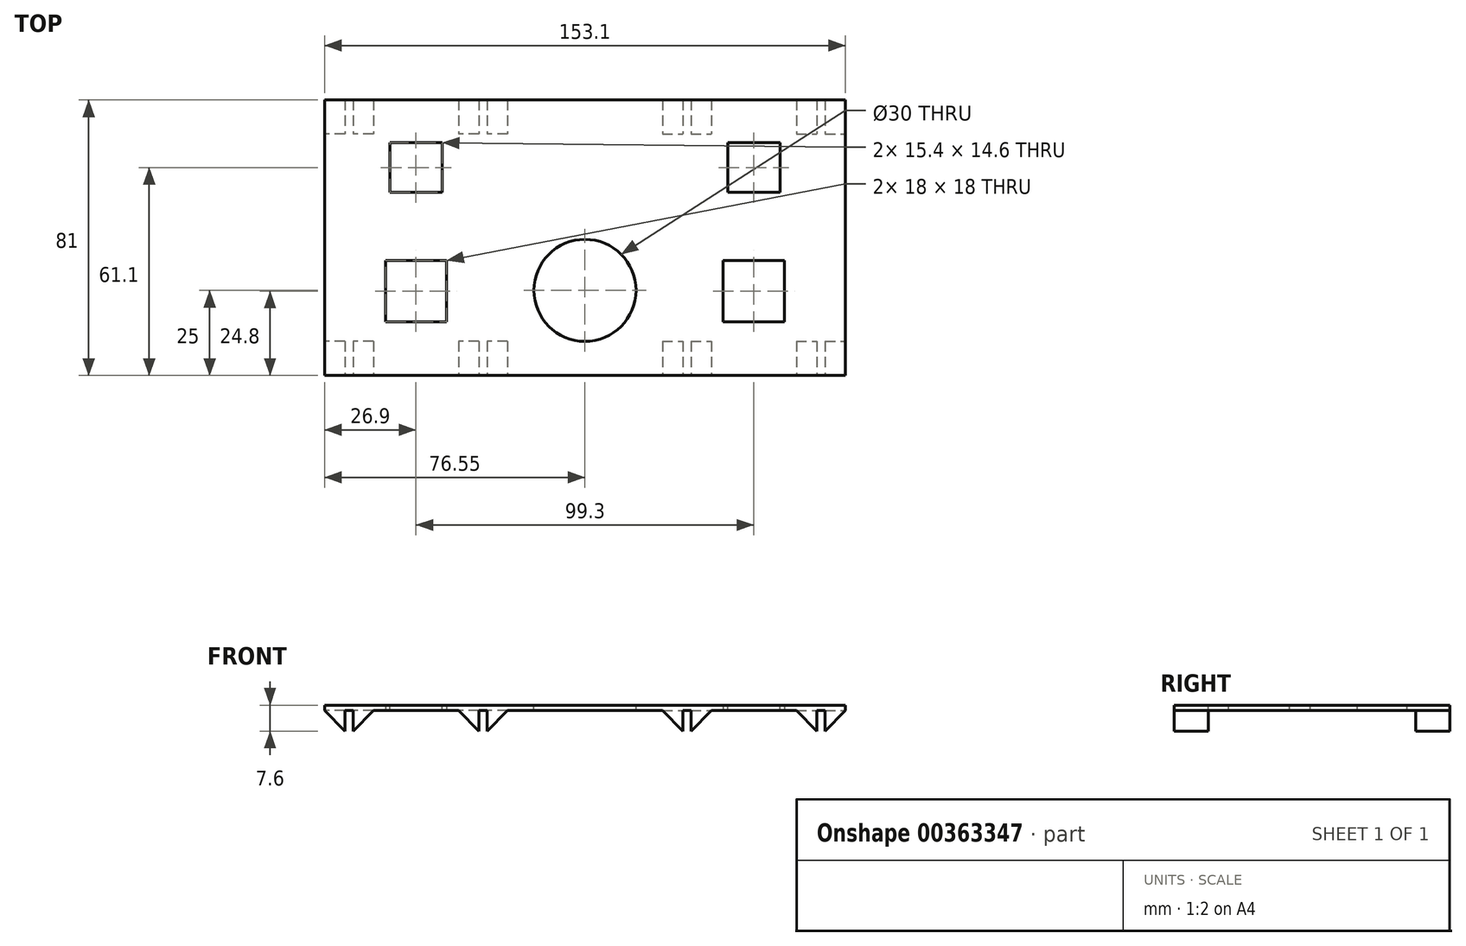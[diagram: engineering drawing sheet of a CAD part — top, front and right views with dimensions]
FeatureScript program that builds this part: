
annotation { "Feature Type Name" : "Feature", "Feature Type Description" : "" }
export const myFeature = defineFeature(function(context is Context, id is Id, definition is map)
    precondition{}
    {
        {
            var Q0;
            Q0=qCreatedBy(makeId("Front.planeOp"),FACE);
            cPlane(context, id + "F0", {"entities" : qUnion([Q0]), "cplaneType" : CPlaneType.OFFSET, "offset" : 40.5 * mm, "width" : 150 * mm, "height" : 150 * mm});
        }
        {
            var Q0;
            Q0=qCreatedBy(id+"F0.planeOp",FACE);
            var sketch = newSketch(context, id + "F1", { "sketchPlane" : qUnion([Q0])});
            skLineSegment(sketch, "E0", {"start": v(76.55, 1.6) * mm, "end": v(76.55, 0) * mm});
            skLineSegment(sketch, "E1", {"start": v(76.55, 0) * mm, "end": v(-76.55, 0) * mm});
            skLineSegment(sketch, "E2", {"start": v(-76.55, 0) * mm, "end": v(-76.55, 1.6) * mm});
            skLineSegment(sketch, "E3", {"start": v(-76.55, 1.6) * mm, "end": v(76.55, 1.6) * mm});
            skLineSegment(sketch, "E4", {"start": v(-70.55, -6) * mm, "end": v(-70.55, 0) * mm});
            skLineSegment(sketch, "E5", {"start": v(-76.55, 0) * mm, "end": v(-70.55, 0) * mm});
            skLineSegment(sketch, "E6", {"start": v(-68.15, 0) * mm, "end": v(-68.15, -6) * mm});
            skLineSegment(sketch, "E7", {"start": v(-62.15, 0) * mm, "end": v(-68.15, 0) * mm});
            skLineSegment(sketch, "E8", {"start": v(-28.75, 0) * mm, "end": v(-28.75, -6) * mm});
            skLineSegment(sketch, "E9", {"start": v(-22.75, 0) * mm, "end": v(-28.75, 0) * mm});
            skLineSegment(sketch, "E10", {"start": v(-31.15, 0) * mm, "end": v(-31.15, -6) * mm});
            skLineSegment(sketch, "E11", {"start": v(-37.15, 0) * mm, "end": v(-31.15, 0) * mm});
            skLineSegment(sketch, "E12.MirrorCS", {"start": v(22.75, -10) * mm, "end": v(22.75, 0) * mm});
            skLineSegment(sketch, "E13.MirrorCS", {"start": v(28.75, 0) * mm, "end": v(28.75, -6) * mm});
            skLineSegment(sketch, "E14.MirrorCS", {"start": v(37.15, -10) * mm, "end": v(37.15, 0) * mm});
            skLineSegment(sketch, "E15.MirrorCS", {"start": v(31.15, 0) * mm, "end": v(31.15, -6) * mm});
            skLineSegment(sketch, "E16.MirrorCS", {"start": v(31.15, -6) * mm, "end": v(32.75, -6) * mm});
            skLineSegment(sketch, "E17.MirrorCS", {"start": v(37.15, 0) * mm, "end": v(31.15, 0) * mm});
            skLineSegment(sketch, "E18.MirrorCS", {"start": v(68.15, 0) * mm, "end": v(68.15, -6) * mm});
            skLineSegment(sketch, "E19.MirrorCS", {"start": v(62.15, -10) * mm, "end": v(62.15, 0) * mm});
            skLineSegment(sketch, "E20.MirrorCS", {"start": v(62.15, 0) * mm, "end": v(68.15, 0) * mm});
            skLineSegment(sketch, "E21.MirrorCS", {"start": v(70.55, -6) * mm, "end": v(70.55, 0) * mm});
            skLineSegment(sketch, "E22.MirrorCS", {"start": v(76.55, 0) * mm, "end": v(70.55, 0) * mm});
            skLineSegment(sketch, "E23.MirrorCS", {"start": v(76.55, 0) * mm, "end": v(76.55, -10) * mm});
            skLineSegment(sketch, "E24.MirrorCS", {"start": v(72.15, -6) * mm, "end": v(70.55, -6) * mm});
            skLineSegment(sketch, "E25.MirrorCS", {"start": v(68.15, -6) * mm, "end": v(66.55, -6) * mm});
            skLineSegment(sketch, "E26.MirrorCS", {"start": v(28.75, -6) * mm, "end": v(27.15, -6) * mm});
            skLineSegment(sketch, "E27", {"start": v(-28.75, 0) * mm, "end": v(-22.75, 0) * mm});
            skLineSegment(sketch, "E28", {"start": v(22.75, 0) * mm, "end": v(28.75, 0) * mm});
            skLineSegment(sketch, "E29", {"start": v(-70.55, -6) * mm, "end": v(-76.55, 0) * mm});
            skLineSegment(sketch, "E30", {"start": v(-62.15, 0) * mm, "end": v(-68.15, -6) * mm});
            skLineSegment(sketch, "E31", {"start": v(-37.15, 0) * mm, "end": v(-31.15, -6) * mm});
            skLineSegment(sketch, "E32", {"start": v(-22.75, 0) * mm, "end": v(-28.75, -6) * mm});
            skSolve(sketch);
        }
        {
            var Q0;
            Q0=makeQuery(id+"F1.imprint","IMPRINT",FACE,{"disambiguationData":[TD([[makeQuery(id+"F1.imprint","IMPRINT",EDGE,{"derivedFrom":sQuery(id+"F1.wireOp",EDGE,"E0")}),-1.0]])]});
            extrude(context, id + "F2", {"entities" : qUnion([Q0]), "oppositeDirection" : true, "depth" : 81 * mm});
        }
        {
            var Q0;
            Q0=makeQuery(id+"F1.imprint","IMPRINT",FACE,{"disambiguationData":[TD([[makeQuery(id+"F1.imprint","IMPRINT",EDGE,{"derivedFrom":sQuery(id+"F1.wireOp",EDGE,"FF6IQarz-4mcM-jOca-ocC3-CsUcrpMwuvCt")}),1.0]])]});
            var Q1;
            Q1=makeQuery(id+"F1.imprint","IMPRINT",FACE,{"disambiguationData":[TD([[makeQuery(id+"F1.imprint","IMPRINT",EDGE,{"derivedFrom":sQuery(id+"F1.wireOp",EDGE,"E6")}),1.0]])]});
            var Q2;
            Q2=makeQuery(id+"F1.imprint","IMPRINT",FACE,{"disambiguationData":[TD([[makeQuery(id+"F1.imprint","IMPRINT",EDGE,{"derivedFrom":sQuery(id+"F1.wireOp",EDGE,"E10")}),-1.0]])]});
            var Q3;
            Q3=makeQuery(id+"F1.imprint","IMPRINT",FACE,{"disambiguationData":[TD([[makeQuery(id+"F1.imprint","IMPRINT",EDGE,{"derivedFrom":sQuery(id+"F1.wireOp",EDGE,"E8")}),1.0]])]});
            var Q4;
            Q4=makeQuery(id+"F1.imprint","IMPRINT",FACE,{"disambiguationData":[TD([[makeQuery(id+"F1.imprint","IMPRINT",EDGE,{"derivedFrom":sQuery(id+"F1.wireOp",EDGE,"E12.MirrorCS")}),-1.0]])]});
            var Q5;
            Q5=makeQuery(id+"F1.imprint","IMPRINT",FACE,{"disambiguationData":[TD([[makeQuery(id+"F1.imprint","IMPRINT",EDGE,{"derivedFrom":sQuery(id+"F1.wireOp",EDGE,"E14.MirrorCS")}),1.0]])]});
            var Q6;
            Q6=makeQuery(id+"F1.imprint","IMPRINT",FACE,{"disambiguationData":[TD([[makeQuery(id+"F1.imprint","IMPRINT",EDGE,{"derivedFrom":sQuery(id+"F1.wireOp",EDGE,"E18.MirrorCS")}),-1.0]])]});
            var Q7;
            Q7=makeQuery(id+"F1.imprint","IMPRINT",FACE,{"disambiguationData":[TD([[makeQuery(id+"F1.imprint","IMPRINT",EDGE,{"derivedFrom":sQuery(id+"F1.wireOp",EDGE,"E21.MirrorCS")}),-1.0]])]});
            var Q8;
            Q8=makeQuery(id+"F1.imprint","IMPRINT",FACE,{"disambiguationData":[TD([[makeQuery(id+"F1.imprint","IMPRINT",EDGE,{"derivedFrom":sQuery(id+"F1.wireOp",EDGE,"E4")}),1.0]])]});
            extrude(context, id + "F3", {"entities" : qUnion([Q0, Q1, Q2, Q3, Q4, Q5, Q6, Q7, Q8]), "operationType" : NewBodyOperationType.ADD, "oppositeDirection" : true, "depth" : 10 * mm});
        }
        {
            var Q0;
            Q0=makeQuery(id+"F1.imprint","IMPRINT",FACE,{"disambiguationData":[TD([[makeQuery(id+"F1.imprint","IMPRINT",EDGE,{"derivedFrom":sQuery(id+"F1.wireOp",EDGE,"FF6IQarz-4mcM-jOca-ocC3-CsUcrpMwuvCt")}),1.0]])]});
            var Q1;
            Q1=makeQuery(id+"F1.imprint","IMPRINT",FACE,{"disambiguationData":[TD([[makeQuery(id+"F1.imprint","IMPRINT",EDGE,{"derivedFrom":sQuery(id+"F1.wireOp",EDGE,"E6")}),1.0]])]});
            var Q2;
            Q2=makeQuery(id+"F1.imprint","IMPRINT",FACE,{"disambiguationData":[TD([[makeQuery(id+"F1.imprint","IMPRINT",EDGE,{"derivedFrom":sQuery(id+"F1.wireOp",EDGE,"E10")}),-1.0]])]});
            var Q3;
            Q3=makeQuery(id+"F1.imprint","IMPRINT",FACE,{"disambiguationData":[TD([[makeQuery(id+"F1.imprint","IMPRINT",EDGE,{"derivedFrom":sQuery(id+"F1.wireOp",EDGE,"E8")}),1.0]])]});
            var Q4;
            Q4=makeQuery(id+"F1.imprint","IMPRINT",FACE,{"disambiguationData":[TD([[makeQuery(id+"F1.imprint","IMPRINT",EDGE,{"derivedFrom":sQuery(id+"F1.wireOp",EDGE,"E14.MirrorCS")}),1.0]])]});
            var Q5;
            Q5=makeQuery(id+"F1.imprint","IMPRINT",FACE,{"disambiguationData":[TD([[makeQuery(id+"F1.imprint","IMPRINT",EDGE,{"derivedFrom":sQuery(id+"F1.wireOp",EDGE,"E12.MirrorCS")}),-1.0]])]});
            var Q6;
            Q6=makeQuery(id+"F1.imprint","IMPRINT",FACE,{"disambiguationData":[TD([[makeQuery(id+"F1.imprint","IMPRINT",EDGE,{"derivedFrom":sQuery(id+"F1.wireOp",EDGE,"E18.MirrorCS")}),-1.0]])]});
            var Q7;
            Q7=makeQuery(id+"F1.imprint","IMPRINT",FACE,{"disambiguationData":[TD([[makeQuery(id+"F1.imprint","IMPRINT",EDGE,{"derivedFrom":sQuery(id+"F1.wireOp",EDGE,"E21.MirrorCS")}),-1.0]])]});
            var Q8;
            Q8=makeQuery(id+"F1.imprint","IMPRINT",FACE,{"disambiguationData":[TD([[makeQuery(id+"F1.imprint","IMPRINT",EDGE,{"derivedFrom":sQuery(id+"F1.wireOp",EDGE,"E4")}),1.0]])]});
            extrude(context, id + "F4", {"entities" : qUnion([Q0, Q1, Q2, Q3, Q4, Q5, Q6, Q7, Q8]), "operationType" : NewBodyOperationType.ADD, "oppositeDirection" : true, "depth" : 81 * mm, "hasSecondDirection" : true, "secondDirectionOppositeDirection" : true, "secondDirectionDepth" : 71 * mm});
        }
        {
            var Q0;
            Q0=qCreatedBy(makeId("Right.planeOp"),FACE);
            cPlane(context, id + "F5", {"entities" : qUnion([Q0]), "cplaneType" : CPlaneType.OFFSET, "offset" : 49.65 * mm, "oppositeDirection" : true, "width" : 150 * mm, "height" : 150 * mm});
        }
        {
            var Q0;
            Q0=qCreatedBy(id+"F5.planeOp",FACE);
            var sketch = newSketch(context, id + "F6", { "sketchPlane" : qUnion([Q0])});
            skLineSegment(sketch, "E33", {"start": v(-13.5, -6) * mm, "end": v(-13.5, 0) * mm});
            skLineSegment(sketch, "E34", {"start": v(-13.5, 0) * mm, "end": v(-7.5, 0) * mm});
            skLineSegment(sketch, "E35", {"start": v(-17.9, 0) * mm, "end": v(-17.9, -6) * mm});
            skLineSegment(sketch, "E36", {"start": v(-23.9, 0) * mm, "end": v(-17.9, 0) * mm});
            skLineSegment(sketch, "E37", {"start": v(-23.9, 0) * mm, "end": v(-17.9, -6) * mm});
            skLineSegment(sketch, "E38", {"start": v(-7.5, 0) * mm, "end": v(-13.5, -6) * mm});
            skSolve(sketch);
        }
        {
            var Q0;
            Q0=makeQuery(id+"F2.opExtrude","SWEPT_BODY",BODY,{"disambiguationData":[OSD([sQuery(id+"F1.wireOp",EDGE,"E0"),sQuery(id+"F1.wireOp",EDGE,"E1"),sQuery(id+"F1.wireOp",EDGE,"E2"),sQuery(id+"F1.wireOp",EDGE,"E3"),sQuery(id+"F1.wireOp",EDGE,"E5"),sQuery(id+"F1.wireOp",EDGE,"E7"),sQuery(id+"F1.wireOp",EDGE,"E11"),sQuery(id+"F1.wireOp",EDGE,"E17.MirrorCS"),sQuery(id+"F1.wireOp",EDGE,"E20.MirrorCS"),sQuery(id+"F1.wireOp",EDGE,"E22.MirrorCS"),sQuery(id+"F1.wireOp",EDGE,"E27"),sQuery(id+"F1.wireOp",EDGE,"E28")])]});
            var Q1;
            Q1=qCreatedBy(makeId("Right.planeOp"),FACE);
            mirror(context, id + "F7", {"operationType" : NewBodyOperationType.ADD, "entities" : qUnion([Q0]), "mirrorPlane" : qUnion([Q1])});
        }
        {
            var Q0;
            Q0=makeQuery(id+"F2.opExtrude","SWEPT_FACE",FACE,{"disambiguationData":[OSD([sQuery(id+"F1.wireOp",EDGE,"E3")])]});
            var sketch = newSketch(context, id + "F8", { "sketchPlane" : qUnion([Q0])});
            skCircle(sketch, "E39", {"center": v(0, -15.5) * mm, "radius": 15 * mm});
            skLineSegment(sketch, "E40", {"start": v(0, -15.5) * mm, "end": v(88.5, -15.5) * mm});
            skSolve(sketch);
        }
        {
            var Q0;
            Q0=qSketchRegion(id+"F8",true);
            extrude(context, id + "F9", {"entities" : qUnion([Q0]), "operationType" : NewBodyOperationType.REMOVE, "oppositeDirection" : true, "depth" : 1.6 * mm});
        }
        {
            var Q0;
            Q0=makeQuery(id+"F2.opExtrude","SWEPT_FACE",FACE,{"disambiguationData":[OSD([sQuery(id+"F1.wireOp",EDGE,"E3")])]});
            var sketch = newSketch(context, id + "F10", { "sketchPlane" : qUnion([Q0])});
            skLineSegment(sketch, "E41.bottom", {"start": v(-57.35, 27.9) * mm, "end": v(-41.95, 27.9) * mm});
            skLineSegment(sketch, "E41.top", {"start": v(-57.35, 13.3) * mm, "end": v(-41.95, 13.3) * mm});
            skLineSegment(sketch, "E41.left", {"start": v(-57.35, 27.9) * mm, "end": v(-57.35, 13.3) * mm});
            skLineSegment(sketch, "E41.right", {"start": v(-41.95, 27.9) * mm, "end": v(-41.95, 13.3) * mm});
            skLineSegment(sketch, "E42.MirrorCS", {"start": v(57.35, 27.9) * mm, "end": v(41.95, 27.9) * mm});
            skLineSegment(sketch, "E43.MirrorCS", {"start": v(41.95, 27.9) * mm, "end": v(41.95, 13.3) * mm});
            skLineSegment(sketch, "E44.MirrorCS", {"start": v(57.35, 13.3) * mm, "end": v(41.95, 13.3) * mm});
            skLineSegment(sketch, "E45.MirrorCS", {"start": v(57.35, 27.9) * mm, "end": v(57.35, 13.3) * mm});
            skSolve(sketch);
        }
        {
            var Q0;
            Q0=qSketchRegion(id+"F10",true);
            extrude(context, id + "F11", {"entities" : qUnion([Q0]), "operationType" : NewBodyOperationType.REMOVE, "oppositeDirection" : true, "depth" : 1.6 * mm});
        }
        {
            var Q0;
            Q0=qCreatedBy(makeId("Top.planeOp"),FACE);
            var sketch = newSketch(context, id + "F12", { "sketchPlane" : qUnion([Q0])});
            skPoint(sketch, "E46", {"position": v(-49.65, -15.7) * mm});
            skLineSegment(sketch, "E47", {"start": v(-58.65, -24.7) * mm, "end": v(-40.65, -24.7) * mm});
            skLineSegment(sketch, "E48", {"start": v(-40.65, -24.7) * mm, "end": v(-40.65, -6.7) * mm});
            skLineSegment(sketch, "E49", {"start": v(-40.65, -6.7) * mm, "end": v(-58.65, -6.7) * mm});
            skLineSegment(sketch, "E50", {"start": v(-58.65, -6.7) * mm, "end": v(-58.65, -24.7) * mm});
            skLineSegment(sketch, "E51.MirrorCS", {"start": v(58.65, -6.7) * mm, "end": v(58.65, -24.7) * mm});
            skLineSegment(sketch, "E52.MirrorCS", {"start": v(58.65, -24.7) * mm, "end": v(40.65, -24.7) * mm});
            skLineSegment(sketch, "E53.MirrorCS", {"start": v(40.65, -6.7) * mm, "end": v(58.65, -6.7) * mm});
            skLineSegment(sketch, "E54.MirrorCS", {"start": v(40.65, -24.7) * mm, "end": v(40.65, -6.7) * mm});
            skSolve(sketch);
        }
        {
            var Q0;
            Q0 = qSketchRegion(id + "F12", true);
            extrude(context, id + "F13", {"entities" : qUnion([Q0]), "operationType" : NewBodyOperationType.REMOVE, "depth" : 1.6 * mm});
        }
    });
